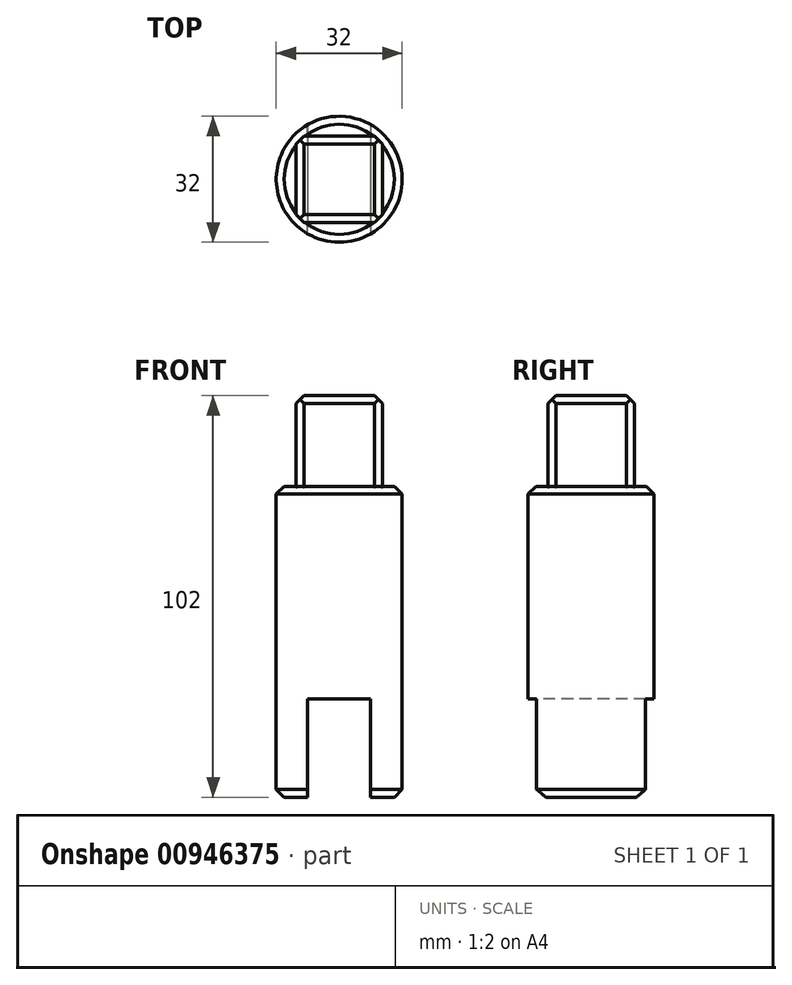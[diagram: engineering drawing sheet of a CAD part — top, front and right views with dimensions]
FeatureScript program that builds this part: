
annotation { "Feature Type Name" : "Feature", "Feature Type Description" : "" }
export const myFeature = defineFeature(function(context is Context, id is Id, definition is map)
    precondition{}
    {
        {
            var Q0;
            Q0=qCreatedBy(makeId("Top.planeOp"),FACE);
            var sketch = newSketch(context, id + "F0", { "sketchPlane" : qUnion([Q0])});
            skCircle(sketch, "E0", {"center": v(0, 0) * mm, "radius": 16 * mm});
            skSolve(sketch);
        }
        {
            var Q0;
            Q0=makeQuery(id+"F0.imprint","IMPRINT",FACE,{"disambiguationData":[TD([[makeQuery(id+"F0.imprint","IMPRINT",EDGE,{"derivedFrom":sQuery(id+"F0.wireOp",EDGE,"E0")}),1.0]])]});
            extrude(context, id + "F1", {"entities" : qUnion([Q0]), "depth" : 79 * mm, "offsetDistance" : 25 * mm});
        }
        {
            var Q0;
            Q0=makeQuery(id+"F1.opExtrude","CAP_FACE",FACE,{"disambiguationData":[OSD([sQuery(id+"F0.wireOp",EDGE,"E0")])],"isStart":false});
            var sketch = newSketch(context, id + "F2", { "sketchPlane" : qUnion([Q0])});
            skLineSegment(sketch, "E1.bottom", {"start": v(10.95, -10.95) * mm, "end": v(-10.95, -10.95) * mm});
            skLineSegment(sketch, "E1.top", {"start": v(10.95, 10.95) * mm, "end": v(-10.95, 10.95) * mm});
            skLineSegment(sketch, "E1.left", {"start": v(10.95, -10.95) * mm, "end": v(10.95, 10.95) * mm});
            skLineSegment(sketch, "E1.right", {"start": v(-10.95, -10.95) * mm, "end": v(-10.95, 10.95) * mm});
            skPoint(sketch, "E1.middle", {"position": v(0, 0) * mm});
            skSolve(sketch);
        }
        {
            var Q0;
            Q0=makeQuery(id+"F2.imprint","IMPRINT",FACE,{"disambiguationData":[TD([[makeQuery(id+"F2.imprint","IMPRINT",EDGE,{"derivedFrom":sQuery(id+"F2.wireOp",EDGE,"E1.bottom")}),-1.0]])]});
            extrude(context, id + "F3", {"entities" : qUnion([Q0]), "operationType" : NewBodyOperationType.ADD, "depth" : 23 * mm, "offsetDistance" : 25 * mm});
        }
        {
            var Q0;
            Q0=makeQuery(id+"F1.opExtrude","CAP_FACE",FACE,{"disambiguationData":[OSD([sQuery(id+"F0.wireOp",EDGE,"E0")])],"isStart":true});
            var sketch = newSketch(context, id + "F4", { "sketchPlane" : qUnion([Q0])});
            skLineSegment(sketch, "E2.bottom", {"start": v(-8, -21.64) * mm, "end": v(8, -21.64) * mm});
            skLineSegment(sketch, "E2.top", {"start": v(-8, 21.64) * mm, "end": v(8, 21.64) * mm});
            skLineSegment(sketch, "E2.left", {"start": v(-8, -21.64) * mm, "end": v(-8, 21.64) * mm});
            skLineSegment(sketch, "E2.right", {"start": v(8, -21.64) * mm, "end": v(8, 21.64) * mm});
            skPoint(sketch, "E2.middle", {"position": v(0, 0) * mm});
            skSolve(sketch);
        }
        {
            var Q0;
            {var subQ0=sQuery(id+"F4.wireOp",EDGE,"E2.top");Q0=makeQuery(id+"F4.imprint","IMPRINT",FACE,{"disambiguationData":[TD([[makeQuery(id+"F4.imprint","IMPRINT",EDGE,{"derivedFrom":subQ0}),-1.0]])]});}
            var Q1;
            {var subQ0=sQuery(id+"F4.wireOp",EDGE,"E2.left");var subQ1=makeQuery(id+"F1.opExtrude","CAP_EDGE",EDGE,{"disambiguationData":[OSD([sQuery(id+"F0.wireOp",EDGE,"E0")])],"isStart":true});var subQ2=makeQuery(id+"F4.imprint","INTERSECT",VERTEX,{"disambiguationData":[OD(0.0)],"derivedFrom":[subQ1,subQ0]});Q1=makeQuery(id+"F4.imprint","IMPRINT",FACE,{"disambiguationData":[TD([[makeQuery(id+"F4.imprint","IMPRINT",EDGE,{"disambiguationData":[TD([[subQ2,-1.0]])],"derivedFrom":subQ0}),-1.0]])]});}
            extrude(context, id + "F5", {"entities" : qUnion([Q0, Q1]), "operationType" : NewBodyOperationType.REMOVE, "oppositeDirection" : true, "depth" : 25 * mm, "offsetDistance" : 25 * mm});
        }
        {
            var Q0;
            Q0=makeQuery(id+"F1.opExtrude","CAP_EDGE",EDGE,{"disambiguationData":[OSD([sQuery(id+"F0.wireOp",EDGE,"E0")])],"isStart":false});
            var Q1;
            Q1=makeQuery(id+"F3.opExtrude","CAP_EDGE",EDGE,{"disambiguationData":[OSD([sQuery(id+"F2.wireOp",EDGE,"E1.bottom")])],"isStart":false});
            var Q2;
            Q2=makeQuery(id+"F3.opExtrude","CAP_EDGE",EDGE,{"disambiguationData":[OSD([sQuery(id+"F2.wireOp",EDGE,"E1.right")])],"isStart":false});
            var Q3;
            Q3=makeQuery(id+"F3.opExtrude","CAP_EDGE",EDGE,{"disambiguationData":[OSD([sQuery(id+"F2.wireOp",EDGE,"E1.top")])],"isStart":false});
            var Q4;
            Q4=makeQuery(id+"F3.opExtrude","CAP_EDGE",EDGE,{"disambiguationData":[OSD([sQuery(id+"F2.wireOp",EDGE,"E1.left")])],"isStart":false});
            chamfer(context, id + "F6", {"entities" : qUnion([Q0, Q1, Q2, Q3, Q4]), "width" : 2 * mm, "tangentPropagation" : true});
        }
        {
            var Q0;
            Q0=makeQuery(id+"F3.opExtrude","SWEPT_EDGE",EDGE,{"disambiguationData":[OSD([sQuery(id+"F2.wireOp",EDGE,"E1.top"),sQuery(id+"F2.wireOp",EDGE,"E1.right")])]});
            var Q1;
            Q1=makeQuery(id+"F3.opExtrude","SWEPT_EDGE",EDGE,{"disambiguationData":[OSD([sQuery(id+"F2.wireOp",EDGE,"E1.bottom"),sQuery(id+"F2.wireOp",EDGE,"E1.right")])]});
            var Q2;
            Q2=makeQuery(id+"F3.opExtrude","SWEPT_EDGE",EDGE,{"disambiguationData":[OSD([sQuery(id+"F2.wireOp",EDGE,"E1.bottom"),sQuery(id+"F2.wireOp",EDGE,"E1.left")])]});
            var Q3;
            Q3=makeQuery(id+"F3.opExtrude","SWEPT_EDGE",EDGE,{"disambiguationData":[OSD([sQuery(id+"F2.wireOp",EDGE,"E1.top"),sQuery(id+"F2.wireOp",EDGE,"E1.left")])]});
            chamfer(context, id + "F7", {"entities" : qUnion([Q0, Q1, Q2, Q3]), "width" : 2 * mm, "tangentPropagation" : true});
        }
        {
            var Q0;
            {var subQ0=sQuery(id+"F0.wireOp",EDGE,"E0");Q0=makeQuery(id+"F5.boolean.opBoolean","SPLIT",EDGE,{"disambiguationData":[TD([makeQuery(id+"F5.opExtrude","SWEPT_FACE",FACE,{"disambiguationData":[OSD([sQuery(id+"F4.wireOp",EDGE,"E2.left")])]})])],"derivedFrom":makeQuery(id+"F1.opExtrude","CAP_EDGE",EDGE,{"disambiguationData":[OSD([subQ0])],"isStart":true})});}
            var Q1;
            {var subQ0=sQuery(id+"F0.wireOp",EDGE,"E0");Q1=makeQuery(id+"F5.boolean.opBoolean","SPLIT",EDGE,{"disambiguationData":[TD([makeQuery(id+"F5.opExtrude","SWEPT_FACE",FACE,{"disambiguationData":[OSD([sQuery(id+"F4.wireOp",EDGE,"E2.right")])]})])],"derivedFrom":makeQuery(id+"F1.opExtrude","CAP_EDGE",EDGE,{"disambiguationData":[OSD([subQ0])],"isStart":true})});}
            chamfer(context, id + "F8", {"entities" : qUnion([Q0, Q1]), "width" : 2 * mm, "tangentPropagation" : true});
        }
    });
